# Revit family: Haworth_Patterns_Worksurface_Key
name_source: partatom
category: Furniture Systems
revit_build: Autodesk Revit 2018 (Build: 20170223_1515(x64)
units: mm (PartAtom-declared; Revit-internal decimal feet)

## family parameters
Always vertical = Yes
Cut with Voids When Loaded = No
OmniClass Number = 23.40.70.14.64.21
OmniClass Title = Systems Furniture
Part Type = Normal
Room Calculation Point = No
Round Connector Dimension = Use Diameter
Shared = No
Work Plane-Based = No

## types (1)
- 48w 36d
    Actual Depth = 36"
    Actual Height = 29"
    Actual Width = 48"
    Assembly Code = E2020200
    Custom Size = No
    Depth = 36"
    Description = Haworth - Worksurface - Patterns - Key
    Disc Base Radius = 10 1/2"
    Disc Base Support = Yes
    Flip-top Location = 4"
    Height = 29"
    Leg Height = 27 13/16"
    Manufacturer = Haworth
    Max. Depth = 48"
    Max. Height = 42"
    Max. Width = 72"
    Min. Depth = 30"
    Min. Height = 22"
    Min. Width = 36"
    Min/Max Depth = 30, 36, 42, 48 in.
    Min/Max Height = 26-32 in.
    Min/Max Width = 48, 60, 72 in.
    Model = Haworth - Worksurface - Patterns - Key
    Revision Number = 3
    Size = Verify Final Dim. w/ Haworth
    Support Column = No
    Support Finish = Haworth _ Paint _ Metallic Champagne
    Sustainability Info = http://www.haworth.com
    Table Thickness = 1 3/16"
    URL = https://www.haworth.com
    URL - Product = https://www.haworth.com
    Warranty = http://www.haworth.com
    Width = 48"
    Worksurface Edge Finish = Haworth _ Wood _ White Oak
    Worksurface Finish = Haworth _ Wood _ White Oak

## geometry (parser evidence)
native form markers: Sweep x10
no freeform markers — native parametric forms only
